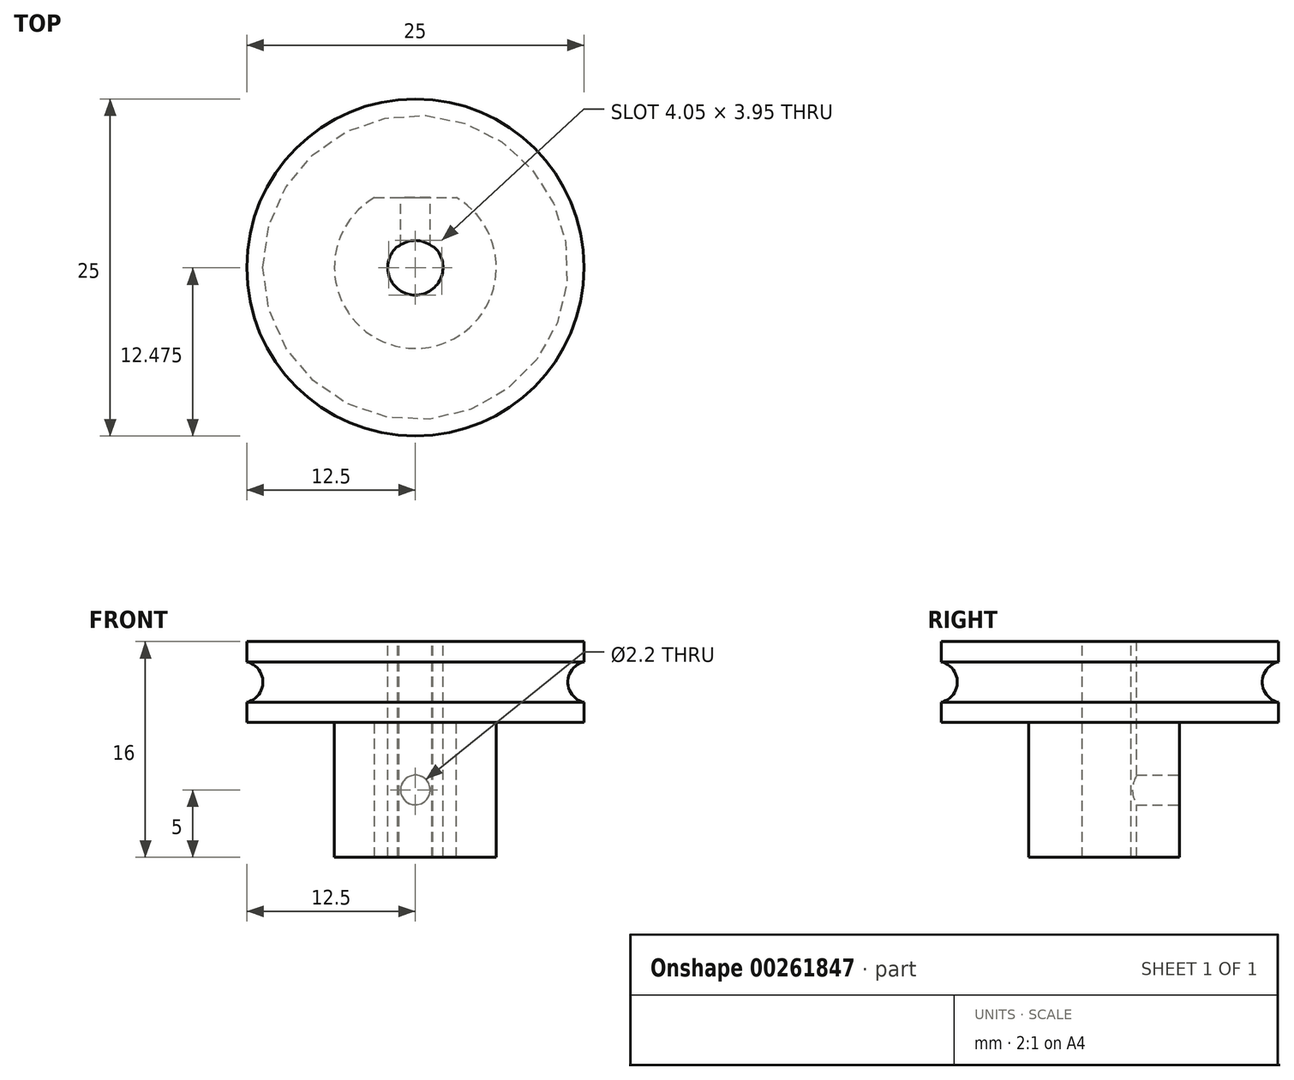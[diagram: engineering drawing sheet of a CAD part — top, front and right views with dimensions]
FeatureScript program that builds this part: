
annotation { "Feature Type Name" : "Feature", "Feature Type Description" : "" }
export const myFeature = defineFeature(function(context is Context, id is Id, definition is map)
    precondition{}
    {
        {
            var Q0;
            Q0=qCreatedBy(makeId("Front.planeOp"),FACE);
            var sketch = newSketch(context, id + "F0", { "sketchPlane" : qUnion([Q0])});
            skLineSegment(sketch, "E0", {"start": v(0, 0) * mm, "end": v(-12.5, 0) * mm});
            skLineSegment(sketch, "E1", {"start": v(-12.5, 0) * mm, "end": v(-12.5, 1.5) * mm});
            skLineSegment(sketch, "E2", {"start": v(0, 3) * mm, "end": v(-18.74, 3) * mm, "construction": true});
            skLineSegment(sketch, "E3.MirrorCS", {"start": v(-12.5, 6) * mm, "end": v(-12.5, 4.5) * mm});
            skLineSegment(sketch, "E4.MirrorCS", {"start": v(0, 6) * mm, "end": v(-12.5, 6) * mm});
            skArc(sketch, "E5", {"start": v(-12.5, 1.5) * mm, "mid": v(-11.3, 3) * mm, "end": v(-12.5, 4.5) * mm});
            skLineSegment(sketch, "E6", {"start": v(0, 0) * mm, "end": v(0, 6) * mm});
            skLineSegment(sketch, "E7", {"start": v(-11.3, 6) * mm, "end": v(-11.3, 0) * mm, "construction": true});
            skSolve(sketch);
        }
        {
            var Q0;
            Q0=qSketchRegion(id+"F0",true);
            var Q1;
            Q1=sQuery(id+"F0.wireOp",EDGE,"E6");
            revolve(context, id + "F1", {"entities" : qUnion([Q0]), "axis" : qUnion([Q1]), "revolveType" : RevolveType.FULL});
        }
        {
            var Q0;
            Q0=makeQuery(id+"F1.opRevolve","SWEPT_FACE",FACE,{"disambiguationData":[OSD([sQuery(id+"F0.wireOp",EDGE,"E4.MirrorCS")])]});
            var sketch = newSketch(context, id + "F2", { "sketchPlane" : qUnion([Q0])});
            skCircle(sketch, "E8", {"center": v(0, 0) * mm, "radius": 2.05 * mm});
            skLineSegment(sketch, "E9", {"start": v(-1.3, 1.58) * mm, "end": v(1.3, 1.58) * mm});
            skArc(sketch, "E10", {"start": v(-1.3, 1.58) * mm, "mid": v(0, -2.05) * mm, "end": v(1.3, 1.58) * mm});
            skSolve(sketch);
        }
        {
            var Q0;
            Q0=qCreatedBy(makeId("Top.planeOp"),FACE);
            var sketch = newSketch(context, id + "F3", { "sketchPlane" : qUnion([Q0])});
            skCircle(sketch, "E11", {"center": v(0, 0) * mm, "radius": 6 * mm, "construction": true});
            skLineSegment(sketch, "E12", {"start": v(-3.04, 5.18) * mm, "end": v(3.04, 5.18) * mm});
            skArc(sketch, "E13", {"start": v(-3.04, 5.18) * mm, "mid": v(0, -6) * mm, "end": v(3.04, 5.18) * mm});
            skSolve(sketch);
        }
        {
            var Q0;
            Q0=makeQuery(id+"F3.imprint","IMPRINT",FACE,{"disambiguationData":[TD([[makeQuery(id+"F3.imprint","IMPRINT",EDGE,{"derivedFrom":sQuery(id+"F3.wireOp",EDGE,"E12")}),-1.0]])]});
            extrude(context, id + "F4", {"entities" : qUnion([Q0]), "operationType" : NewBodyOperationType.ADD, "oppositeDirection" : true, "depth" : 10 * mm});
        }
        {
            var Q0;
            Q0=makeQuery(id+"F2.imprint","IMPRINT",FACE,{"disambiguationData":[TD([[makeQuery(id+"F2.imprint","IMPRINT",EDGE,{"derivedFrom":sQuery(id+"F2.wireOp",EDGE,"E9")}),-1.0]])]});
            extrude(context, id + "F5", {"entities" : qUnion([Q0]), "operationType" : NewBodyOperationType.REMOVE, "endBound" : BoundingType.THROUGH_ALL, "oppositeDirection" : true, "depth" : 25 * mm});
        }
        {
            var Q0;
            Q0=makeQuery(id+"F4.opExtrude","SWEPT_FACE",FACE,{"disambiguationData":[OSD([sQuery(id+"F3.wireOp",EDGE,"E12")])]});
            var sketch = newSketch(context, id + "F6", { "sketchPlane" : qUnion([Q0])});
            skLineSegment(sketch, "E14", {"start": v(3.04, -10) * mm, "end": v(-3.04, 0) * mm, "construction": true});
            skLineSegment(sketch, "E15", {"start": v(-3.04, 0) * mm, "end": v(3.04, 0) * mm, "construction": true});
            skLineSegment(sketch, "E16", {"start": v(3.04, 0) * mm, "end": v(-3.04, -10) * mm, "construction": true});
            skPoint(sketch, "E17", {"position": v(0, -5) * mm});
            skSolve(sketch);
        }
        {
            var Q0;
            Q0=sQuery(id+"F6.wireOp",VERTEX,"E17");
            var Q1;
            Q1=makeQuery(id+"F1.opRevolve","SWEPT_BODY",BODY,{"disambiguationData":[OSD([sQuery(id+"F0.wireOp",EDGE,"E0"),sQuery(id+"F0.wireOp",EDGE,"E1"),sQuery(id+"F0.wireOp",EDGE,"E3.MirrorCS"),sQuery(id+"F0.wireOp",EDGE,"E4.MirrorCS"),sQuery(id+"F0.wireOp",EDGE,"E5"),sQuery(id+"F0.wireOp",EDGE,"E6")])]});
            hole(context, id + "F7", {"style" : HoleStyle.SIMPLE, "endStyle" : HoleEndStyle.BLIND, "holeDiameter" : 2.2 * mm, "holeDepth" : 4 * mm, "tappedDepth" : 12 * mm, "tapClearance" : 3, "locations" : qUnion([Q0]), "scope" : qUnion([Q1])});
        }
        {
            var Q0;
            Q0=sQuery(id+"F2.wireOp",VERTEX,"E10.center");
            var Q1;
            Q1=makeQuery(id+"F1.opRevolve","SWEPT_BODY",BODY,{"disambiguationData":[OSD([sQuery(id+"F0.wireOp",EDGE,"E0"),sQuery(id+"F0.wireOp",EDGE,"E1"),sQuery(id+"F0.wireOp",EDGE,"E3.MirrorCS"),sQuery(id+"F0.wireOp",EDGE,"E4.MirrorCS"),sQuery(id+"F0.wireOp",EDGE,"E5"),sQuery(id+"F0.wireOp",EDGE,"E6")])]});
            hole(context, id + "F8", {"style" : HoleStyle.SIMPLE, "endStyle" : HoleEndStyle.THROUGH, "holeDiameter" : 4 * mm, "tappedDepth" : 12 * mm, "tapClearance" : 3, "locations" : qUnion([Q0]), "scope" : qUnion([Q1])});
        }
    });
